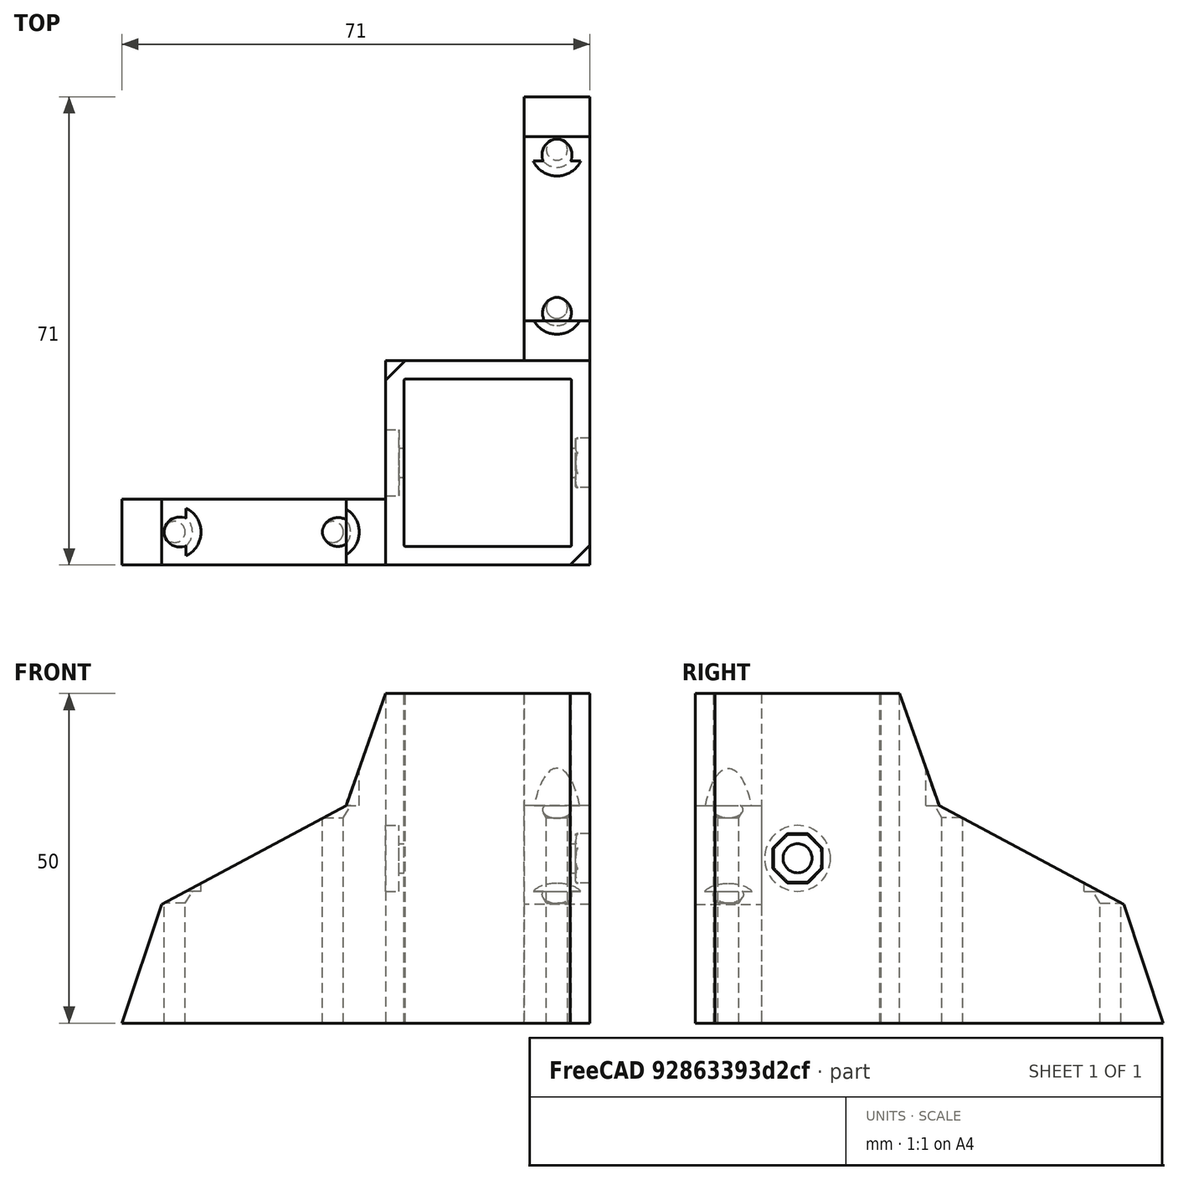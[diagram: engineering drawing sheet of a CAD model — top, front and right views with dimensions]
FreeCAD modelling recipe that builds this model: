
FCSTD DOCUMENT  (FreeCAD 0.19R24276 (Git))
Label: escuadra_tabla_inferior
License: All rights reserved
LicenseURL: http://en.wikipedia.org/wiki/All_rights_reserved
objects: TechDraw::DrawViewDimension×11, Part::Offset×7, Part::MultiFuse×7, Part::Cylinder×6, Part::Cut×5, TechDraw::DrawProjGroupItem×3, Part::Box×2, Part::Cone×2, Sketcher::SketchObject×2, PartDesign::Pad×2, TechDraw::DrawSVGTemplate×2, TechDraw::DrawViewPart×2, TechDraw::DrawPage×2, Part::Feature×1, PartDesign::FeatureBase×1, PartDesign::Body×1, Part::Chamfer×1, TechDraw::DrawProjGroup×1, TechDraw::DrawViewAnnotation×1
note: 39 computed .brp shape members not serialized (recipe doc carries the construction recipe); baked Part::Feature solids carry a one-line shape summary decoded from their .brp

FEATURE [Part::Box] Box  label="Cubo"
  AttacherType = Attacher::AttachEngine3D
  Height = 70
  Length = 25
  Width = 25
FEATURE [Part::Box] Box001  label="Cubo001"
  AttacherType = Attacher::AttachEngine3D
  Height = 50
  Length = 31
  Placement = pos=(-3,-3,0) rot=(0,0,1;0rad)
  Width = 31
FEATURE [Part::Offset] Offset
  Fill = false
  Intersection = false
  Join = 0
  Mode = 0
  SelfIntersection = false
  Source = -> Box
  Value = 0.2
FEATURE [Part::Cylinder] Cylinder  label="Cilindro"
  Angle = 360
  AttacherType = Attacher::AttachEngine3D
  Height = 35
  Placement = pos=(-3,12.5,25) rot=(0,1,0;1.5708rad)
  Radius = 2
FEATURE [Part::Feature] Part__Feature  label="Chamfer"
  Placement = pos=(26,12.5,25) rot=(0,1,0;1.5708rad)
  shape: bbox 3.203 x 7.66 x 7.66 mm, 15 faces (baked)
FEATURE [Part::Offset] Offset002
  Fill = false
  Intersection = false
  Join = 0
  Mode = 0
  SelfIntersection = false
  Source = -> Part__Feature
  Value = 0.2
FEATURE [Part::Cut] Cut
  Base = -> Box001
  Tool = -> Offset
FEATURE [Part::Offset] Offset003
  Fill = false
  Intersection = false
  Join = 0
  Mode = 0
  SelfIntersection = false
  Source = -> Cylinder
  Value = 0.2
FEATURE [Part::Cut] Cut001
  Base = -> Cut
  Tool = -> Offset003
FEATURE [Part::Cut] Cut002
  Base = -> Cut001
  Tool = -> Offset002
FEATURE [Part::Cylinder] Cylinder001  label="Cilindro001"
  Angle = 360
  AttacherType = Attacher::AttachEngine3D
  Height = 2
  Placement = pos=(-3,12.5,25) rot=(0,1,0;1.5708rad)
  Radius = 5
FEATURE [Part::Cut] Cut003
  Base = -> Cut002
  Tool = -> Cylinder001
FEATURE [PartDesign::FeatureBase] BaseFeature
  BaseFeature = -> Cut003
FEATURE [Part::Cylinder] Cylinder002  label="Cilindro002"
  Angle = 360
  AttacherType = Attacher::AttachEngine3D
  Height = 20
  Placement = pos=(-35,2,0) rot=(0,0,1;0rad)
  Radius = 1.5
FEATURE [Part::Cylinder] Cylinder003  label="Cilindro003"
  Angle = 360
  AttacherType = Attacher::AttachEngine3D
  Height = 33
  Placement = pos=(-11,2,0) rot=(0,0,1;0rad)
  Radius = 1.5
FEATURE [Part::Cylinder] Cylinder006  label="Cilindro006"
  Angle = 360
  AttacherType = Attacher::AttachEngine3D
  Height = 7
  Placement = pos=(-11,2,33) rot=(0,0,1;0rad)
  Radius = 4
FEATURE [Part::Cylinder] Cylinder007  label="Cilindro007"
  Angle = 360
  AttacherType = Attacher::AttachEngine3D
  Height = 7
  Placement = pos=(-35,2,20) rot=(0,0,1;0rad)
  Radius = 4
FEATURE [Part::Cone] Cone  label="Cono"
  Angle = 360
  AttacherType = Attacher::AttachEngine3D
  Height = 2
  Placement = pos=(-11,2,36) rot=(0,0,1;0rad)
  Radius1 = 1.25
  Radius2 = 2.5
FEATURE [Part::Cone] Cone001  label="Cono001"
  Angle = 360
  AttacherType = Attacher::AttachEngine3D
  Height = 2
  Placement = pos=(-35,2,6) rot=(0,0,1;0rad)
  Radius1 = 1.25
  Radius2 = 2.5
FEATURE [Part::Offset] Offset004
  Fill = false
  Intersection = false
  Join = 0
  Mode = 0
  Placement = pos=(0,0,-5) rot=(0,0,1;0rad)
  SelfIntersection = false
  Source = -> Cone
  Value = 0.2
FEATURE [Part::Offset] Offset005
  Fill = false
  Intersection = false
  Join = 0
  Mode = 0
  Placement = pos=(0,0,12) rot=(0,0,1;0rad)
  SelfIntersection = false
  Source = -> Cone001
  Value = 0.2
FEATURE [Sketcher::SketchObject] Sketch
  ExternalGeometry = -> [BaseFeature]
  FullyConstrained = false
  MapMode = 5
  Placement = pos=(28,0,0) rot=(0.57735,0.57735,0.57735;2.0944rad)
  Support = -> [BaseFeature]
  sketch-geometry (7):
    g0: LineSegment StartX=68 StartY=5.4e-15 StartZ=0 EndX=28 EndY=0 EndZ=0
    g1: LineSegment StartX=28 StartY=0 StartZ=0 EndX=28 EndY=50 EndZ=0
    g2: LineSegment StartX=34 StartY=8e-16 StartZ=0 EndX=34 EndY=33 EndZ=0
    g3: LineSegment StartX=62 StartY=18 StartZ=0 EndX=62 EndY=3.6e-15 EndZ=0
    g4: LineSegment StartX=28 StartY=50 StartZ=0 EndX=34 EndY=33 EndZ=0
    g5: LineSegment StartX=34 StartY=33 StartZ=0 EndX=62 EndY=18 EndZ=0
    g6: LineSegment StartX=62 StartY=18 StartZ=0 EndX=68 EndY=7.1e-15 EndZ=0
  constraints (19):
    c: Coincident(g0,g1)
    c: Coincident(g0,g-3)
    c: DistanceX(g0,g0) = 40
    c: Angle(g0,g1) = 1.5708
    c: PointOnObject(g2,g0)
    c: Vertical(g2)
    c: DistanceY(g2,g2) = 33
    c: Vertical(g3)
    c: PointOnObject(g3,g0)
    c: DistanceY(g3,g3) = 18
    c: DistanceX(g0,g2) = 6
    c: DistanceX(g3,g0) = 6
    c: Coincident(g4,g5)
    c: Coincident(g5,g6)
    c: Coincident(g4,g1)
    c: Coincident(g4,g2)
    c: Coincident(g5,g3)
    c: Coincident(g6,g0)
    c: Coincident(g-3,g1)
FEATURE [PartDesign::Pad] Pad
  AllowMultiFace = false
  BaseFeature = -> BaseFeature
  Direction = (1,1,1)
  Length = 10
  Length2 = 100
  Profile = -> Sketch
  Reversed = true
  Type = 0
FEATURE [Sketcher::SketchObject] Sketch001
  ExternalGeometry = -> [Pad]
  FullyConstrained = false
  MapMode = 5
  Placement = pos=(0,-3,0) rot=(1,0,0;1.5708rad)
  sketch-geometry (7):
    g0: LineSegment StartX=-43 StartY=0 StartZ=0 EndX=-3 EndY=0 EndZ=0
    g1: LineSegment StartX=-3 StartY=50 StartZ=0 EndX=-3 EndY=0 EndZ=0
    g2: LineSegment StartX=-37 StartY=0 StartZ=0 EndX=-37 EndY=18 EndZ=0
    g3: LineSegment StartX=-9 StartY=0 StartZ=0 EndX=-9 EndY=33 EndZ=0
    g4: LineSegment StartX=-3 StartY=50 StartZ=0 EndX=-9 EndY=33 EndZ=0
    g5: LineSegment StartX=-9 StartY=33 StartZ=0 EndX=-37 EndY=18 EndZ=0
    g6: LineSegment StartX=-37 StartY=18 StartZ=0 EndX=-43 EndY=0 EndZ=0
  constraints (19):
    c: DistanceX(g0,g0) = 40
    c: Coincident(g1,g0)
    c: Coincident(g1,g-3)
    c: Vertical(g2)
    c: Vertical(g3)
    c: PointOnObject(g2,g0)
    c: Horizontal(g0)
    c: Coincident(g0,g-3)
    c: PointOnObject(g3,g0)
    c: DistanceY(g3,g3) = 33
    c: DistanceY(g2,g2) = 18
    c: DistanceX(g3,g0) = 6
    c: DistanceX(g0,g2) = 6
    c: Coincident(g4,g5)
    c: Coincident(g5,g6)
    c: Coincident(g4,g3)
    c: Coincident(g5,g2)
    c: Coincident(g0,g6)
    c: Coincident(g4,g1)
FEATURE [PartDesign::Pad] Pad001
  AllowMultiFace = false
  BaseFeature = -> Pad
  Direction = (1,1,1)
  Length = 10
  Length2 = 100
  Profile = -> Sketch001
  Reversed = true
  Type = 0
FEATURE [PartDesign::Body] Body
  BaseFeature = -> Cut003
  Group = -> [BaseFeature,Sketch,Sketch001,Pad,Pad001]
  Origin = -> Origin
  Tip = -> Pad001
FEATURE [Part::Offset] Offset006
  Fill = false
  Intersection = false
  Join = 0
  Mode = 0
  SelfIntersection = false
  Source = -> Cylinder003
  Value = 0.1
FEATURE [Part::MultiFuse] Fusion
  Shapes = -> [Offset004,Offset006]
FEATURE [Part::MultiFuse] Fusion001
  Shapes = -> [Cylinder006,Fusion]
FEATURE [Part::Offset] Offset007
  Fill = false
  Intersection = false
  Join = 0
  Mode = 0
  SelfIntersection = false
  Source = -> Cylinder002
  Value = 0.1
FEATURE [Part::MultiFuse] Fusion002
  Shapes = -> [Offset007,Offset005]
FEATURE [Part::MultiFuse] Fusion003
  Shapes = -> [Fusion002,Cylinder007]
FEATURE [Part::MultiFuse] Fusion004
  Shapes = -> [Fusion001,Fusion003]
FEATURE [Part::MultiFuse] Fusion005
  Placement = pos=(21,25,0) rot=(0,0,-1;1.5708rad)
  Shapes = -> [Fusion001,Fusion003]
FEATURE [Part::MultiFuse] Fusion006
  Shapes = -> [Fusion004,Fusion005]
FEATURE [Part::Cut] Cut004
  Base = -> Pad001
  Tool = -> Fusion006
FEATURE [Part::Chamfer] Chamfer  label="Chamfer001"
  Base = -> Cut004
  Edges = 2 edges r=3: [Edge70,Edge89]
FEATURE [TechDraw::DrawSVGTemplate] Template
  EditableTexts = Designed_by_Name=<owner>; Drawing_number=001; FC-Date=-; FC-SC=1:2; FC-SH=1/2; FC-Title=WoodPlatformBase; Subtitle=Apoyo Plataforma Madera; Weight=<100gr
  Height = 210
  Orientation = 1
  Width = 297
FEATURE [TechDraw::DrawSVGTemplate] Template001
  EditableTexts = Designed_by_Name=<owner>; Drawing_number=001; FC-Date=-; FC-SC=1:1; FC-SH=2/2; FC-Title=WoodPlatformBase; Subtitle=Apoyo Plataforma Madera; Weight=<100gr
  Height = 210
  Orientation = 1
  Width = 297
FEATURE [TechDraw::DrawViewPart] View
  CoarseView = false
  Direction = (0.577,-0.577,0.577)
  Focus = 100
  HardHidden = false
  IsoCount = 0
  IsoHidden = false
  IsoVisible = false
  LockPosition = false
  Perspective = false
  Rotation = 0
  ScaleType = 0
  SeamHidden = false
  SeamVisible = true
  SmoothHidden = false
  SmoothVisible = true
  Source = -> [Chamfer]
  X = 156.1
  XDirection = (0.707,0.707,0)
  Y = 128.2
FEATURE [TechDraw::DrawProjGroupItem] ProjItem  label="Front"
  CoarseView = false
  Direction = (0,-1,0)
  Focus = 100
  HardHidden = false
  IsoCount = 0
  IsoHidden = false
  IsoVisible = false
  LockPosition = true
  Perspective = false
  Rotation = 0
  RotationVector = (1,0,0)
  Scale = 0.5
  ScaleType = 2
  SeamHidden = false
  SeamVisible = true
  SmoothHidden = false
  SmoothVisible = true
  Source = -> [Chamfer]
  Type = 0
  X = 0
  XDirection = (1,0,0)
  Y = 0
FEATURE [TechDraw::DrawProjGroupItem] ProjItem001  label="Right"
  CoarseView = false
  Direction = (1,-1e-16,0)
  Focus = 100
  HardHidden = false
  IsoCount = 0
  IsoHidden = false
  IsoVisible = false
  LockPosition = false
  Perspective = false
  Rotation = 0
  RotationVector = (1,0,0)
  Scale = 0.5
  ScaleType = 2
  SeamHidden = false
  SeamVisible = true
  SmoothHidden = false
  SmoothVisible = true
  Source = -> [Chamfer]
  Type = 2
  X = -50.5
  XDirection = (1e-16,1,0)
  Y = 0
FEATURE [TechDraw::DrawProjGroupItem] ProjItem002  label="Top"
  CoarseView = false
  Direction = (0,0,1)
  Focus = 100
  HardHidden = false
  IsoCount = 0
  IsoHidden = false
  IsoVisible = false
  LockPosition = false
  Perspective = false
  Rotation = 0
  RotationVector = (1,0,0)
  Scale = 0.5
  ScaleType = 2
  SeamHidden = false
  SeamVisible = true
  SmoothHidden = false
  SmoothVisible = true
  Source = -> [Chamfer]
  Type = 4
  X = 0
  XDirection = (1,0,0)
  Y = -50.5
FEATURE [TechDraw::DrawProjGroup] ProjGroup
  Anchor = -> ProjItem
  AutoDistribute = true
  LockPosition = false
  ProjectionType = 0
  Rotation = 0
  Scale = 0.5
  ScaleType = 2
  Source = -> [Chamfer]
  Views = -> [ProjItem,ProjItem001,ProjItem002]
  X = 104.5
  Y = 143.4
  spacingX = 15
  spacingY = 15
FEATURE [TechDraw::DrawViewPart] View001
  CoarseView = false
  Direction = (0.577,-0.577,0.577)
  Focus = 100
  HardHidden = false
  IsoCount = 0
  IsoHidden = false
  IsoVisible = false
  LockPosition = false
  Perspective = false
  Rotation = 0
  ScaleType = 0
  SeamHidden = false
  SeamVisible = true
  SmoothHidden = false
  SmoothVisible = true
  Source = -> [Chamfer]
  X = 212.9
  XDirection = (0.707,0.707,0)
  Y = 124.2
FEATURE [TechDraw::DrawViewDimension] Dimension
  Arbitrary = false
  ArbitraryTolerances = false
  EqualTolerance = true
  FormatSpec = %.2f
  FormatSpecOverTolerance = %+.2f
  FormatSpecUnderTolerance = %+.2f
  Inverted = false
  LockPosition = false
  MeasureType = 1
  OverTolerance = 0
  References2D = -> [ProjItem]
  Rotation = 0
  ScaleType = 0
  TheoreticalExact = false
  Type = 1
  UnderTolerance = 0
  X = 0
  Y = -14.7505
FEATURE [TechDraw::DrawViewDimension] Dimension001
  Arbitrary = false
  ArbitraryTolerances = false
  EqualTolerance = true
  FormatSpec = %.2f
  FormatSpecOverTolerance = %+.2f
  FormatSpecUnderTolerance = %+.2f
  Inverted = false
  LockPosition = false
  MeasureType = 1
  OverTolerance = 0
  References2D = -> [ProjItem]
  Rotation = 0
  ScaleType = 0
  TheoreticalExact = false
  Type = 2
  UnderTolerance = 0
  X = 17.75
  Y = 2.57202
FEATURE [TechDraw::DrawViewDimension] Dimension003
  Arbitrary = false
  ArbitraryTolerances = false
  EqualTolerance = true
  FormatSpec = %.2f
  FormatSpecOverTolerance = %+.2f
  FormatSpecUnderTolerance = %+.2f
  Inverted = false
  LockPosition = false
  MeasureType = 1
  OverTolerance = 0
  References2D = -> [ProjItem002]
  Rotation = 0
  ScaleType = 0
  TheoreticalExact = false
  Type = 1
  UnderTolerance = 0
  X = 39.7389
  Y = -16.9698
FEATURE [TechDraw::DrawViewDimension] Dimension004
  Arbitrary = false
  ArbitraryTolerances = false
  EqualTolerance = true
  FormatSpec = %.2f
  FormatSpecOverTolerance = %+.2f
  FormatSpecUnderTolerance = %+.2f
  Inverted = false
  LockPosition = false
  MeasureType = 1
  OverTolerance = 0
  References2D = -> [ProjItem002]
  Rotation = 0
  ScaleType = 0
  TheoreticalExact = false
  Type = 2
  UnderTolerance = 0
  X = -12.0572
  Y = 17.4616
FEATURE [TechDraw::DrawViewDimension] Dimension005
  Arbitrary = false
  ArbitraryTolerances = false
  EqualTolerance = true
  FormatSpec = ⌀%.2f
  FormatSpecOverTolerance = %+.2f
  FormatSpecUnderTolerance = %+.2f
  Inverted = false
  LockPosition = false
  MeasureType = 1
  OverTolerance = 0
  References2D = -> [ProjItem001]
  Rotation = 0
  ScaleType = 0
  TheoreticalExact = false
  Type = 5
  UnderTolerance = 0
  X = -28.8734
  Y = 11.8041
FEATURE [TechDraw::DrawViewDimension] Dimension006
  Arbitrary = false
  ArbitraryTolerances = false
  EqualTolerance = true
  FormatSpec = ⌀%.2f
  FormatSpecOverTolerance = %+.2f
  FormatSpecUnderTolerance = %+.2f
  Inverted = false
  LockPosition = false
  MeasureType = 1
  OverTolerance = 0
  References2D = -> [ProjItem002]
  Rotation = 0
  ScaleType = 0
  TheoreticalExact = false
  Type = 5
  UnderTolerance = 0
  X = -28.3173
  Y = -1.50738
FEATURE [TechDraw::DrawPage] Page  label="Vistas"
  KeepUpdated = true
  NextBalloonIndex = 1
  ProjectionType = 0
  Template = -> Template
  Views = -> [ProjGroup,View001,Dimension,Dimension001,Dimension003,Dimension004,Dimension005,Dimension006]
FEATURE [TechDraw::DrawViewDimension] Dimension007
  Arbitrary = false
  ArbitraryTolerances = false
  EqualTolerance = true
  FormatSpec = %.2f
  FormatSpecOverTolerance = %+.2f
  FormatSpecUnderTolerance = %+.2f
  Inverted = false
  LockPosition = false
  MeasureType = 1
  OverTolerance = 0
  References2D = -> [View]
  Rotation = 0
  ScaleType = 0
  TheoreticalExact = false
  Type = 0
  UnderTolerance = 0
  X = 36.0624
  Y = -12.2474
FEATURE [TechDraw::DrawViewDimension] Dimension008
  Arbitrary = false
  ArbitraryTolerances = false
  EqualTolerance = true
  FormatSpec = %.2f
  FormatSpecOverTolerance = %+.2f
  FormatSpecUnderTolerance = %+.2f
  Inverted = false
  LockPosition = false
  MeasureType = 1
  OverTolerance = 0
  References2D = -> [View]
  Rotation = 0
  ScaleType = 0
  TheoreticalExact = false
  Type = 0
  UnderTolerance = 0
  X = 48.0205
  Y = 17.7294
FEATURE [TechDraw::DrawViewDimension] Dimension009
  Arbitrary = false
  ArbitraryTolerances = false
  EqualTolerance = true
  FormatSpec = %.2f
  FormatSpecOverTolerance = %+.2f
  FormatSpecUnderTolerance = %+.2f
  Inverted = false
  LockPosition = false
  MeasureType = 1
  OverTolerance = 0
  References2D = -> [View]
  Rotation = 0
  ScaleType = 0
  TheoreticalExact = false
  Type = 0
  UnderTolerance = 0
  X = 8.87346
  Y = -34.3511
FEATURE [TechDraw::DrawViewDimension] Dimension010
  Arbitrary = false
  ArbitraryTolerances = false
  EqualTolerance = true
  FormatSpec = %.2f
  FormatSpecOverTolerance = %+.2f
  FormatSpecUnderTolerance = %+.2f
  Inverted = false
  LockPosition = false
  MeasureType = 1
  OverTolerance = 0
  References2D = -> [View]
  Rotation = 0
  ScaleType = 0
  TheoreticalExact = false
  Type = 0
  UnderTolerance = 0
  X = -39.3819
  Y = -18.6074
FEATURE [TechDraw::DrawViewDimension] Dimension011
  Arbitrary = false
  ArbitraryTolerances = false
  EqualTolerance = true
  FormatSpec = %.2f
  FormatSpecOverTolerance = %+.2f
  FormatSpecUnderTolerance = %+.2f
  Inverted = false
  LockPosition = false
  MeasureType = 1
  OverTolerance = 0
  References2D = -> [View]
  Rotation = 0
  ScaleType = 0
  TheoreticalExact = false
  Type = 0
  UnderTolerance = 0
  X = -29.4343
  Y = 41.3845
FEATURE [TechDraw::DrawViewAnnotation] Annotation
  Font = osifont
  LineSpace = 80
  LockPosition = false
  MaxWidth = -1
  Rotation = 0
  ScaleType = 0
  Text = Aproximate measurements: | Check with 3D piece
  TextSize = 5
  TextStyle = 0
  X = 86.5
  Y = 71
FEATURE [TechDraw::DrawPage] Page001  label="Cotas"
  KeepUpdated = true
  NextBalloonIndex = 1
  ProjectionType = 0
  Template = -> Template001
  Views = -> [View,Dimension007,Dimension008,Dimension009,Dimension010,Dimension011,Annotation]
